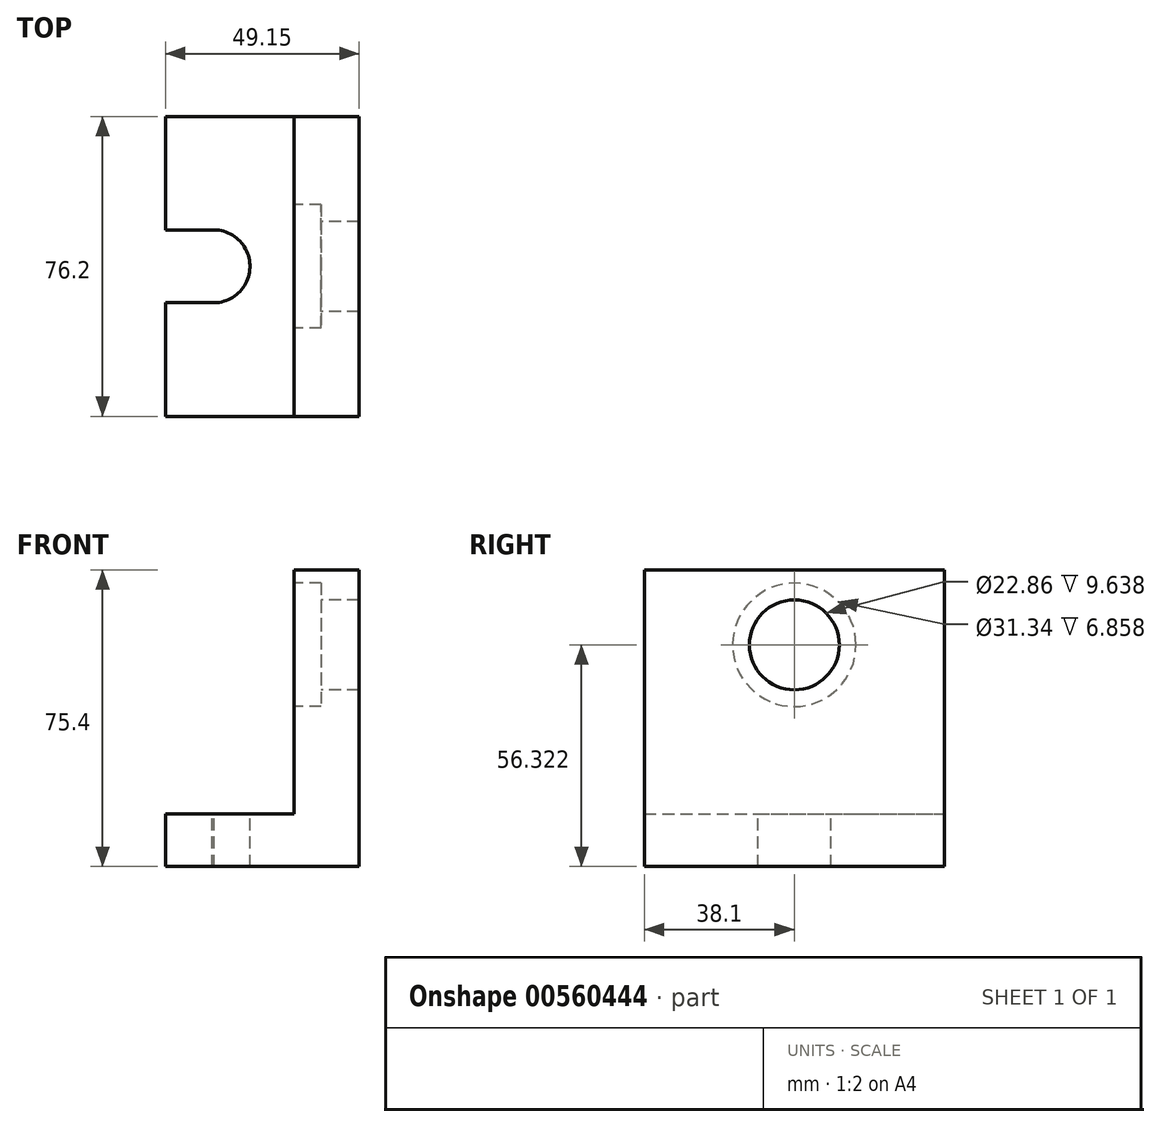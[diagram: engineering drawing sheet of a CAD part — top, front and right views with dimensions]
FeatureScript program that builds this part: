
annotation { "Feature Type Name" : "Feature", "Feature Type Description" : "" }
export const myFeature = defineFeature(function(context is Context, id is Id, definition is map)
    precondition{}
    {
        {
            var Q0;
            Q0=qCreatedBy(makeId("Front.planeOp"),FACE);
            var sketch = newSketch(context, id + "F0", { "sketchPlane" : qUnion([Q0])});
            skLineSegment(sketch, "E0", {"start": v(0, 0) * mm, "end": v(0, 75.4) * mm});
            skLineSegment(sketch, "E1", {"start": v(0, 0) * mm, "end": v(-49.15, 0) * mm});
            skLineSegment(sketch, "E2", {"start": v(-49.15, 0) * mm, "end": v(-49.15, 13.43) * mm});
            skLineSegment(sketch, "E3", {"start": v(-49.15, 13.43) * mm, "end": v(-16.48, 13.43) * mm});
            skLineSegment(sketch, "E4", {"start": v(-16.5, 11.9) * mm, "end": v(-16.5, 75.4) * mm});
            skLineSegment(sketch, "E5", {"start": v(-16.5, 75.4) * mm, "end": v(0, 75.4) * mm});
            skSolve(sketch);
        }
        {
            var Q0;
            Q0=makeQuery(id+"F0.imprint","IMPRINT",FACE,{"disambiguationData":[TD([[makeQuery(id+"F0.imprint","IMPRINT",EDGE,{"derivedFrom":sQuery(id+"F0.wireOp",EDGE,"E0")}),1.0]])]});
            extrude(context, id + "F1", {"entities" : qUnion([Q0]), "endBound" : BoundingType.SYMMETRIC, "depth" : 76.2 * mm, "offsetDistance" : 25.4 * mm});
        }
        {
            var Q0;
            Q0=makeQuery(id+"F1.opExtrude","SWEPT_FACE",FACE,{"disambiguationData":[OSD([sQuery(id+"F0.wireOp",EDGE,"E4")])]});
            var sketch = newSketch(context, id + "F2", { "sketchPlane" : qUnion([Q0])});
            skCircle(sketch, "E6", {"center": v(0, 56.32) * mm, "radius": 11.43 * mm});
            skPoint(sketch, "E6.centerSnap0", {"position": v(0, 75.4) * mm});
            skSolve(sketch);
        }
        {
            var Q0;
            Q0=makeQuery(id+"F2.imprint","IMPRINT",FACE,{"disambiguationData":[TD([[makeQuery(id+"F2.imprint","IMPRINT",EDGE,{"derivedFrom":sQuery(id+"F2.wireOp",EDGE,"E6")}),1.0]])]});
            extrude(context, id + "F3", {"entities" : qUnion([Q0]), "operationType" : NewBodyOperationType.REMOVE, "endBound" : BoundingType.UP_TO_NEXT, "oppositeDirection" : true, "depth" : 25.4 * mm, "offsetDistance" : 25.4 * mm});
        }
        {
            var Q0;
            Q0=makeQuery(id+"F1.opExtrude","SWEPT_FACE",FACE,{"disambiguationData":[OSD([sQuery(id+"F0.wireOp",EDGE,"E4")])]});
            var sketch = newSketch(context, id + "F4", { "sketchPlane" : qUnion([Q0])});
            skCircle(sketch, "E7", {"center": v(0, 56.32) * mm, "radius": 15.67 * mm});
            skSolve(sketch);
        }
        {
            var Q0;
            Q0=makeQuery(id+"F4.imprint","IMPRINT",FACE,{"disambiguationData":[TD([[makeQuery(id+"F4.imprint","IMPRINT",EDGE,{"derivedFrom":sQuery(id+"F4.wireOp",EDGE,"E7")}),1.0]])]});
            extrude(context, id + "F5", {"entities" : qUnion([Q0]), "operationType" : NewBodyOperationType.REMOVE, "oppositeDirection" : true, "depth" : 6.86 * mm, "offsetDistance" : 25.4 * mm});
        }
        {
            var Q0;
            Q0=makeQuery(id+"F1.opExtrude","SWEPT_FACE",FACE,{"disambiguationData":[OSD([sQuery(id+"F0.wireOp",EDGE,"E3")])]});
            var sketch = newSketch(context, id + "F6", { "sketchPlane" : qUnion([Q0])});
            skCircle(sketch, "E8", {"center": v(-37, 0) * mm, "radius": 9.27 * mm});
            skPoint(sketch, "E8.centerSnap0", {"position": v(-16.5, 0) * mm});
            skLineSegment(sketch, "E9", {"start": v(-36.8, 9.27) * mm, "end": v(-49.15, 9.27) * mm});
            skLineSegment(sketch, "E10", {"start": v(-37.37, -9.26) * mm, "end": v(-49.15, -9.26) * mm});
            skSolve(sketch);
        }
        {
            var Q0;
            {var subQ0=sQuery(id+"F6.wireOp",EDGE,"E8");var subQ1=makeQuery(id+"F6.imprint","INTERSECT",VERTEX,{"derivedFrom":[subQ0,sQuery(id+"F6.wireOp",EDGE,"E10")]});Q0=makeQuery(id+"F6.imprint","IMPRINT",FACE,{"disambiguationData":[TD([[makeQuery(id+"F6.imprint","IMPRINT",EDGE,{"disambiguationData":[TD([[subQ1,1.0]])],"derivedFrom":subQ0}),1.0]])]});}
            var Q1;
            {var subQ0=sQuery(id+"F6.wireOp",EDGE,"E10");Q1=makeQuery(id+"F6.imprint","IMPRINT",FACE,{"disambiguationData":[TD([[makeQuery(id+"F6.imprint","IMPRINT",EDGE,{"derivedFrom":subQ0}),-1.0]])]});}
            extrude(context, id + "F7", {"entities" : qUnion([Q0, Q1]), "operationType" : NewBodyOperationType.REMOVE, "endBound" : BoundingType.UP_TO_NEXT, "oppositeDirection" : true, "depth" : 25.4 * mm, "offsetDistance" : 25.4 * mm});
        }
    });
